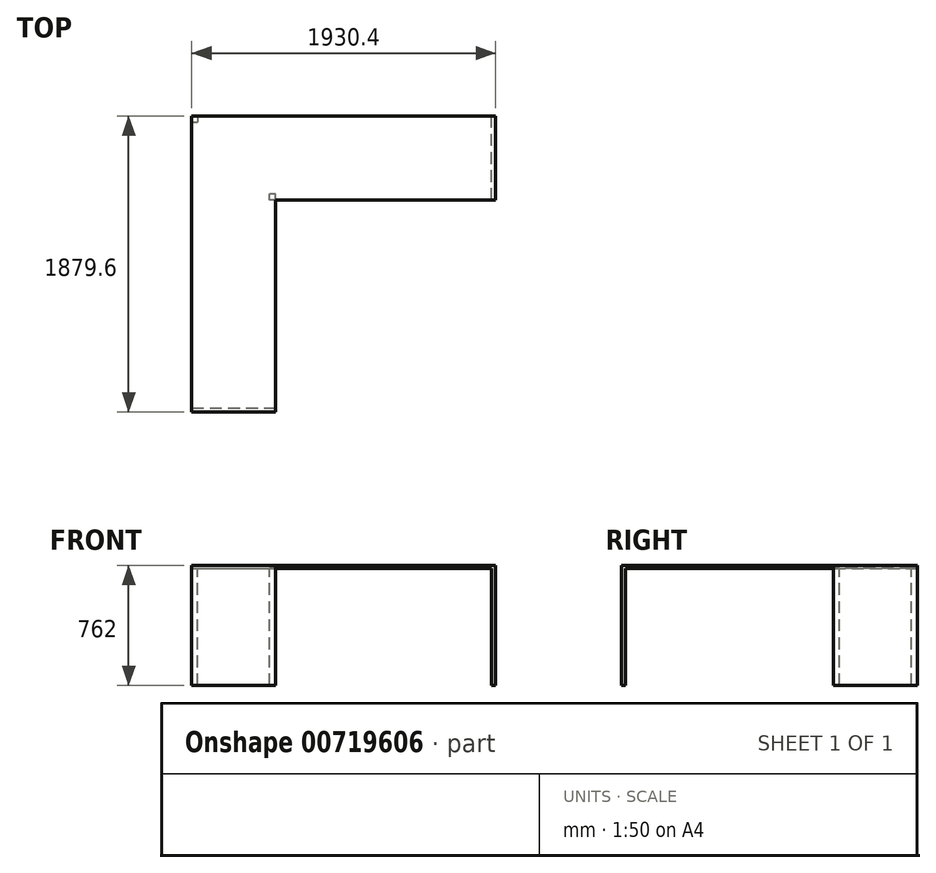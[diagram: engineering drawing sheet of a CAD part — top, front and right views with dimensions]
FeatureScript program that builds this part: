
annotation { "Feature Type Name" : "Feature", "Feature Type Description" : "" }
export const myFeature = defineFeature(function(context is Context, id is Id, definition is map)
    precondition{}
    {
        {
            var Q0;
            Q0=qCreatedBy(makeId("Top.planeOp"),FACE);
            cPlane(context, id + "F0", {"entities" : qUnion([Q0]), "cplaneType" : CPlaneType.OFFSET, "offset" : 762 * mm, "width" : 152.4 * mm, "height" : 152.4 * mm});
        }
        {
            var Q0;
            Q0=qCreatedBy(id+"F0.planeOp",FACE);
            var sketch = newSketch(context, id + "F1", { "sketchPlane" : qUnion([Q0])});
            skLineSegment(sketch, "E0.bottom", {"start": v(0, 0) * mm, "end": v(1930.4, 0) * mm});
            skLineSegment(sketch, "E0.top", {"start": v(533.4, -533.4) * mm, "end": v(1930.4, -533.4) * mm});
            skLineSegment(sketch, "E0.left", {"start": v(0, 0) * mm, "end": v(0, -533.4) * mm});
            skLineSegment(sketch, "E0.right", {"start": v(1930.4, 0) * mm, "end": v(1930.4, -533.4) * mm});
            skLineSegment(sketch, "E1.top", {"start": v(0, -1879.6) * mm, "end": v(533.4, -1879.6) * mm});
            skLineSegment(sketch, "E1.left", {"start": v(0, -533.4) * mm, "end": v(0, -1879.6) * mm});
            skLineSegment(sketch, "E1.right", {"start": v(533.4, -533.4) * mm, "end": v(533.4, -1879.6) * mm});
            skSolve(sketch);
        }
        {
            var Q0;
            Q0 = qSketchRegion(id + "F1", true);
            extrude(context, id + "F2", {"entities" : qUnion([Q0]), "oppositeDirection" : true, "depth" : 19.05 * mm, "offsetDistance" : 25.4 * mm});
        }
        {
            var Q0;
            Q0=makeQuery(id+"F2.opExtrude","CAP_FACE",FACE,{"disambiguationData":[OSD([sQuery(id+"F1.wireOp",EDGE,"E0.bottom"),sQuery(id+"F1.wireOp",EDGE,"E0.top"),sQuery(id+"F1.wireOp",EDGE,"E0.left"),sQuery(id+"F1.wireOp",EDGE,"E0.right"),sQuery(id+"F1.wireOp",EDGE,"E1.top"),sQuery(id+"F1.wireOp",EDGE,"E1.left"),sQuery(id+"F1.wireOp",EDGE,"E1.right")])],"isStart":false});
            var sketch = newSketch(context, id + "F3", { "sketchPlane" : qUnion([Q0])});
            skLineSegment(sketch, "E2.bottom", {"start": v(0, 1879.6) * mm, "end": v(533.4, 1879.6) * mm});
            skLineSegment(sketch, "E2.top", {"start": v(0, 1854.2) * mm, "end": v(533.4, 1854.2) * mm});
            skLineSegment(sketch, "E2.left", {"start": v(0, 1879.6) * mm, "end": v(0, 1854.2) * mm});
            skLineSegment(sketch, "E2.right", {"start": v(533.4, 1879.6) * mm, "end": v(533.4, 1854.2) * mm});
            skLineSegment(sketch, "E3.bottom", {"start": v(1930.4, 533.4) * mm, "end": v(1905, 533.4) * mm});
            skLineSegment(sketch, "E3.top", {"start": v(1930.4, 0) * mm, "end": v(1905, 0) * mm});
            skLineSegment(sketch, "E3.left", {"start": v(1930.4, 533.4) * mm, "end": v(1930.4, 0) * mm});
            skLineSegment(sketch, "E3.right", {"start": v(1905, 533.4) * mm, "end": v(1905, 0) * mm});
            skLineSegment(sketch, "E4.bottom", {"start": v(533.4, 533.4) * mm, "end": v(495.3, 533.4) * mm});
            skLineSegment(sketch, "E4.top", {"start": v(533.4, 495.3) * mm, "end": v(495.3, 495.3) * mm});
            skLineSegment(sketch, "E4.left", {"start": v(533.4, 533.4) * mm, "end": v(533.4, 495.3) * mm});
            skLineSegment(sketch, "E4.right", {"start": v(495.3, 533.4) * mm, "end": v(495.3, 495.3) * mm});
            skLineSegment(sketch, "E5.bottom", {"start": v(0, 0) * mm, "end": v(38.1, 0) * mm});
            skLineSegment(sketch, "E5.top", {"start": v(0, 38.1) * mm, "end": v(38.1, 38.1) * mm});
            skLineSegment(sketch, "E5.left", {"start": v(0, 0) * mm, "end": v(0, 38.1) * mm});
            skLineSegment(sketch, "E5.right", {"start": v(38.1, 0) * mm, "end": v(38.1, 38.1) * mm});
            skSolve(sketch);
        }
        {
            var Q0;
            Q0 = qSketchRegion(id + "F3", true);
            var Q1;
            Q1=qCreatedBy(makeId("Top.planeOp"),FACE);
            extrude(context, id + "F4", {"entities" : qUnion([Q0]), "operationType" : NewBodyOperationType.ADD, "endBound" : BoundingType.UP_TO_SURFACE, "depth" : 25.4 * mm, "endBoundEntityFace" : qUnion([Q1]), "offsetDistance" : 25.4 * mm});
        }
    });
